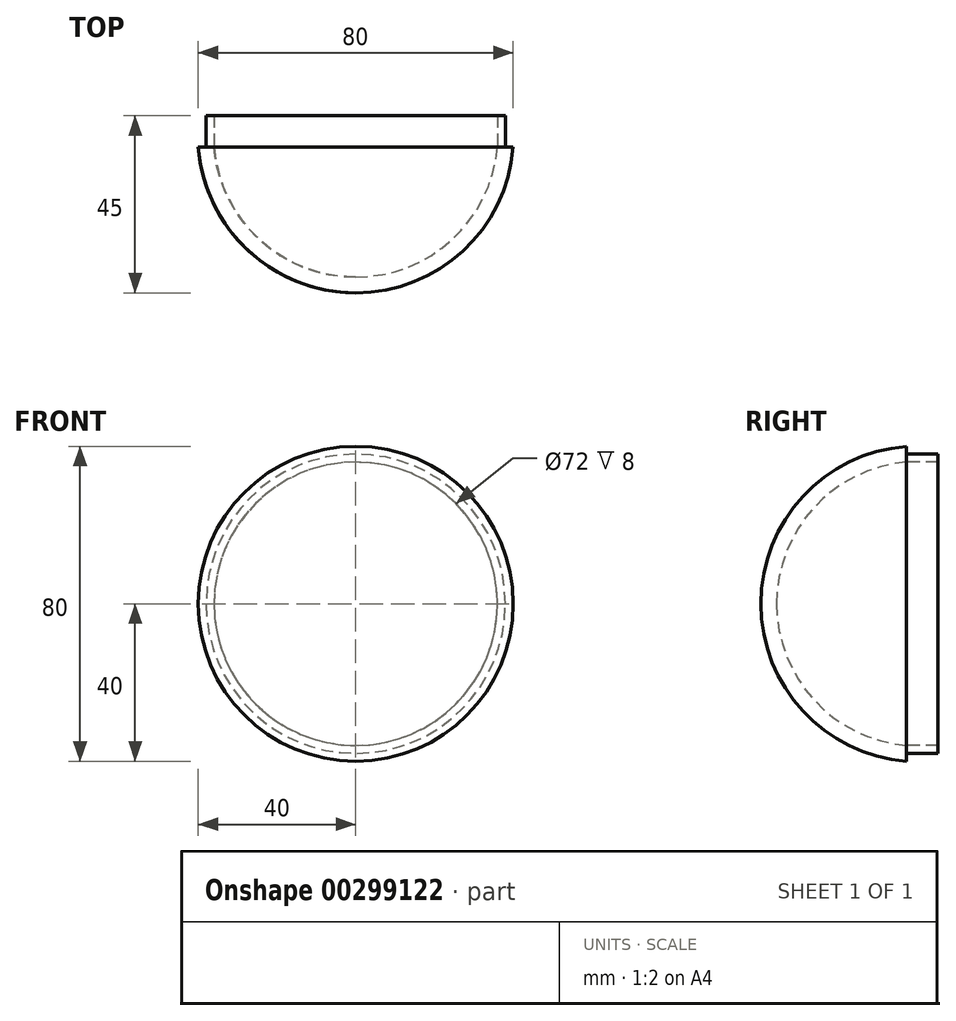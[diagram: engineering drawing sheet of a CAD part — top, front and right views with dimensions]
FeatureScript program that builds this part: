
annotation { "Feature Type Name" : "Feature", "Feature Type Description" : "" }
export const myFeature = defineFeature(function(context is Context, id is Id, definition is map)
    precondition{}
    {
        {
            var Q0;
            Q0=qCreatedBy(makeId("Top.planeOp"),FACE);
            var sketch = newSketch(context, id + "F0", { "sketchPlane" : qUnion([Q0])});
            skLineSegment(sketch, "E0", {"start": v(0, 0) * mm, "end": v(36, 0) * mm});
            skLineSegment(sketch, "E1", {"start": v(0, 0) * mm, "end": v(-36, 0) * mm});
            skLineSegment(sketch, "E2", {"start": v(36, 0) * mm, "end": v(40, 0) * mm});
            skLineSegment(sketch, "E3", {"start": v(-36, 0) * mm, "end": v(-40, 0) * mm});
            skLineSegment(sketch, "E4", {"start": v(0, 0) * mm, "end": v(0, -33) * mm});
            skLineSegment(sketch, "E5", {"start": v(0, -33) * mm, "end": v(0, -37) * mm});
            skArc(sketch, "E6", {"start": v(-36, 0) * mm, "mid": v(0, -33) * mm, "end": v(36, 0) * mm});
            skArc(sketch, "E7", {"start": v(-40, 0) * mm, "mid": v(0, -37) * mm, "end": v(40, 0) * mm});
            skSolve(sketch);
        }
        {
            var Q0;
            {var subQ0=sQuery(id+"F0.wireOp",EDGE,"E3");Q0=makeQuery(id+"F0.imprint","IMPRINT",FACE,{"disambiguationData":[TD([[makeQuery(id+"F0.imprint","IMPRINT",EDGE,{"derivedFrom":subQ0}),1.0]])]});}
            var Q1;
            Q1=sQuery(id+"F0.wireOp",EDGE,"E5");
            revolve(context, id + "F1", {"entities" : qUnion([Q0]), "axis" : qUnion([Q1]), "revolveType" : RevolveType.SYMMETRIC, "angle" : 360 * degree});
        }
        {
            var Q0;
            Q0=makeQuery(id+"F1.opRevolve","SWEPT_FACE",FACE,{"disambiguationData":[OSD([sQuery(id+"F0.wireOp",EDGE,"E3")])]});
            var sketch = newSketch(context, id + "F2", { "sketchPlane" : qUnion([Q0])});
            skCircle(sketch, "E8", {"center": v(0, 0) * mm, "radius": 36 * mm});
            skCircle(sketch, "E9", {"center": v(0, 0) * mm, "radius": 38 * mm});
            skSolve(sketch);
        }
        {
            var Q0;
            Q0=makeQuery(id+"F2.imprint","IMPRINT",FACE,{"disambiguationData":[TD([[makeQuery(id+"F2.imprint","IMPRINT",EDGE,{"derivedFrom":sQuery(id+"F2.wireOp",EDGE,"E8")}),-1.0]])]});
            extrude(context, id + "F3", {"entities" : qUnion([Q0]), "operationType" : NewBodyOperationType.ADD, "depth" : 8 * mm});
        }
    });
